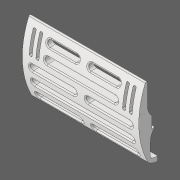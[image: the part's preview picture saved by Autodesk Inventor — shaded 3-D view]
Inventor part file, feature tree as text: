
AUTODESK INVENTOR PART (.ipt)
format: ipt  version: 2020 (Build 240168000, 168)  size: 640,000 bytes
history: native  units: in
note: dims shown in document units (in); Inventor stores cm internally (conversion verified against a paired STEP export)
features: other x4, extrude x3, fillet x2
ambient origin geometry x8: Origin, YZ Plane, XZ Plane, XY Plane, X Axis, Y Axis, Z Axis, Center Point
bodies: Solid1 (feature_tree)
feature tree (9):
  extrude  "Mounting Slots"  TaperAngle=0.0deg  [1 undecoded]
  extrude  "Strap Slots"  Depth=0.0591in
  fillet  "Strap Slot Fillet"  Radius=0.5906in
  extrude  "Cosmetic Slots"  Depth=0.0118in
  fillet  "Cosmetic Slot Fillet"  Radius=0.0118in
  other  "Profile"
  other  "Slot Sketch"
  other  "Strap Slot Sketch"
  other  "Cosmetic Slot Sketch"
note: 1 required parameter value undecoded (feature->parameter linkage not recoverable at this tier; creation-order binding heuristic only, values carry confidence <= 0.55)
